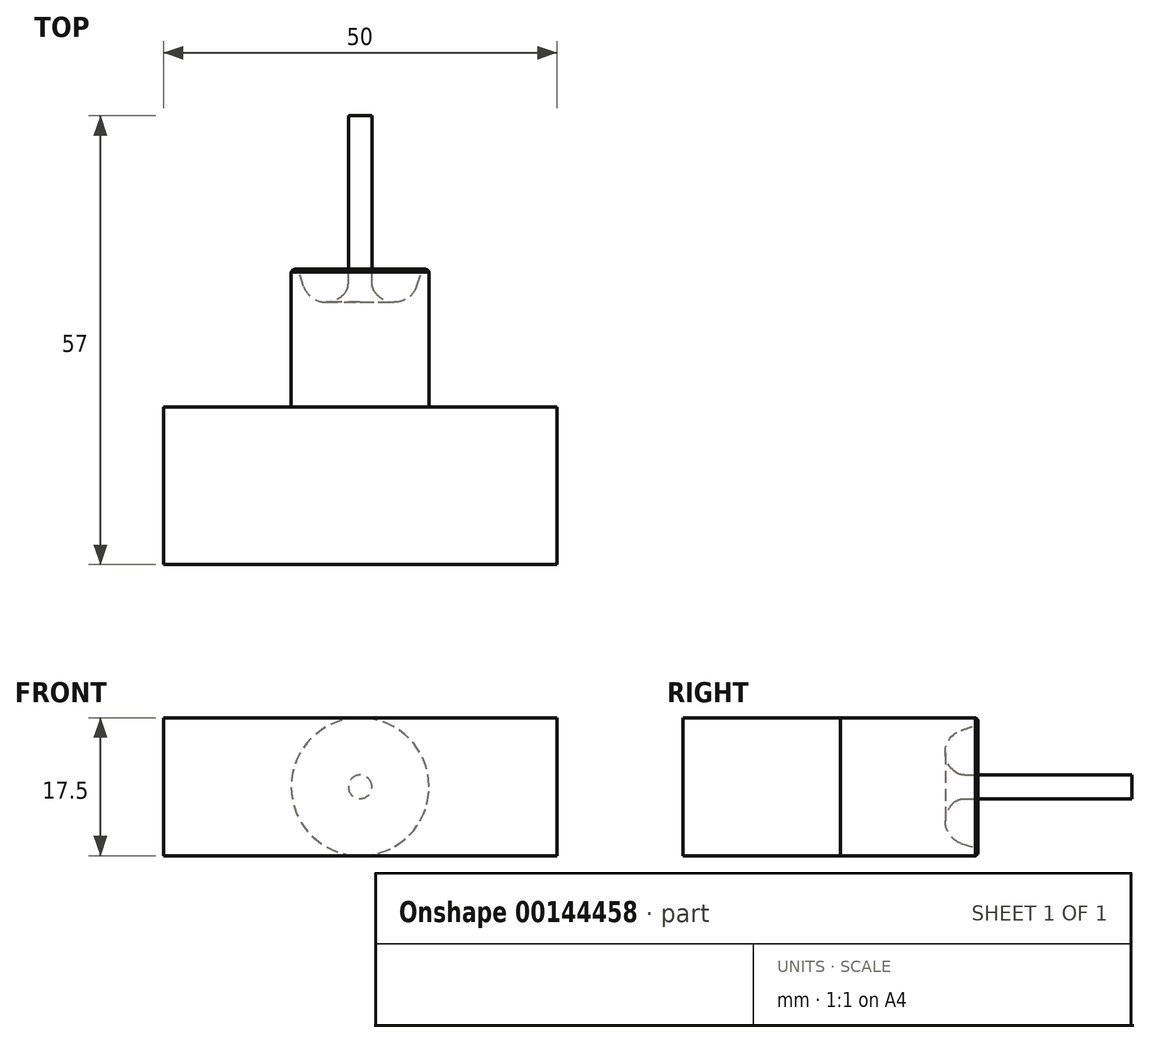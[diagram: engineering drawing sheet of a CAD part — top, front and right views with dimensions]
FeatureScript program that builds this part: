
annotation { "Feature Type Name" : "Feature", "Feature Type Description" : "" }
export const myFeature = defineFeature(function(context is Context, id is Id, definition is map)
    precondition{}
    {
        {
            var Q0;
            Q0=qCreatedBy(makeId("Top.planeOp"),FACE);
            var sketch = newSketch(context, id + "F0", { "sketchPlane" : qUnion([Q0])});
            skLineSegment(sketch, "E0", {"start": v(0, 0) * mm, "end": v(0, 8.99) * mm, "construction": true});
            skLineSegment(sketch, "E1", {"start": v(0, 0) * mm, "end": v(-8.75, 0) * mm});
            skLineSegment(sketch, "E2", {"start": v(-8.75, 0) * mm, "end": v(-8.75, 17.16) * mm});
            skArc(sketch, "E3", {"start": v(-7.8, 17.16) * mm, "mid": v(-8.28, 17.5) * mm, "end": v(-8.75, 17.16) * mm});
            skArc(sketch, "E4", {"start": v(-7.16, 15.33) * mm, "mid": v(-4.33, 13.32) * mm, "end": v(-1.5, 15.33) * mm});
            skLineSegment(sketch, "E5", {"start": v(-1.5, 15.33) * mm, "end": v(-1.5, 37) * mm});
            skLineSegment(sketch, "E6", {"start": v(-1.5, 37) * mm, "end": v(0, 37) * mm});
            skLineSegment(sketch, "E7", {"start": v(0, 37) * mm, "end": v(0, 0) * mm});
            skLineSegment(sketch, "E8", {"start": v(-7.8, 17.16) * mm, "end": v(-7.16, 15.33) * mm});
            skSolve(sketch);
        }
        {
            var Q0;
            Q0=makeQuery(id+"F0.imprint","IMPRINT",FACE,{"disambiguationData":[TD([[makeQuery(id+"F0.imprint","IMPRINT",EDGE,{"derivedFrom":sQuery(id+"F0.wireOp",EDGE,"E1")}),-1.0]])]});
            var Q1;
            Q1=sQuery(id+"F0.wireOp",EDGE,"E7");
            revolve(context, id + "F1", {"entities" : qUnion([Q0]), "axis" : qUnion([Q1]), "revolveType" : RevolveType.FULL});
        }
        {
            var Q0;
            Q0=makeQuery(id+"F1.opRevolve","SWEPT_EDGE",EDGE,{"disambiguationData":[OSD([sQuery(id+"F0.wireOp",EDGE,"E4"),sQuery(id+"F0.wireOp",EDGE,"E5")])]});
            fillet(context, id + "F2", {"entities" : qUnion([Q0]), "radius" : 2 * mm, "tangentPropagation" : true, "allowEdgeOverflow" : false});
        }
        {
            var Q0;
            Q0=makeQuery(id+"F1.opRevolve","SWEPT_FACE",FACE,{"disambiguationData":[OSD([sQuery(id+"F0.wireOp",EDGE,"E1")])]});
            var sketch = newSketch(context, id + "F3", { "sketchPlane" : qUnion([Q0])});
            skLineSegment(sketch, "E9.bottom", {"start": v(-25, 8.75) * mm, "end": v(25, 8.75) * mm});
            skLineSegment(sketch, "E9.top", {"start": v(-25, -8.75) * mm, "end": v(25, -8.75) * mm});
            skLineSegment(sketch, "E9.left", {"start": v(-25, 8.75) * mm, "end": v(-25, -8.75) * mm});
            skLineSegment(sketch, "E9.right", {"start": v(25, 8.75) * mm, "end": v(25, -8.75) * mm});
            skLineSegment(sketch, "E10", {"start": v(0, 0) * mm, "end": v(8.75, 0) * mm});
            skLineSegment(sketch, "E11", {"start": v(0, 0) * mm, "end": v(0, -3.36) * mm});
            skSolve(sketch);
        }
        {
            var Q0;
            {var subQ0=sQuery(id+"F3.wireOp",EDGE,"E9.left");Q0=makeQuery(id+"F3.imprint","IMPRINT",FACE,{"disambiguationData":[TD([[makeQuery(id+"F3.imprint","IMPRINT",EDGE,{"derivedFrom":subQ0}),1.0]])]});}
            var Q1;
            {var subQ4=sQuery(id+"F3.wireOp",EDGE,"E9.right");Q1=makeQuery(id+"F3.imprint","IMPRINT",FACE,{"disambiguationData":[TD([[makeQuery(id+"F3.imprint","IMPRINT",EDGE,{"derivedFrom":subQ4}),-1.0]])]});}
            var Q2;
            {var subQ0=makeQuery(id+"F1.opRevolve","SWEPT_EDGE",EDGE,{"disambiguationData":[OSD([sQuery(id+"F0.wireOp",EDGE,"E1"),sQuery(id+"F0.wireOp",EDGE,"E2")])]});var subQ3=makeQuery(id+"F3.imprint","IMPRINT",VERTEX,{"derivedFrom":subQ0});Q2=makeQuery(id+"F3.imprint","IMPRINT",FACE,{"disambiguationData":[TD([[makeQuery(id+"F3.imprint","IMPRINT",EDGE,{"disambiguationData":[TD([[subQ3,1.0]])],"derivedFrom":subQ0}),-1.0]])]});}
            extrude(context, id + "F4", {"entities" : qUnion([Q0, Q1, Q2]), "operationType" : NewBodyOperationType.ADD, "depth" : 20 * mm});
        }
    });
